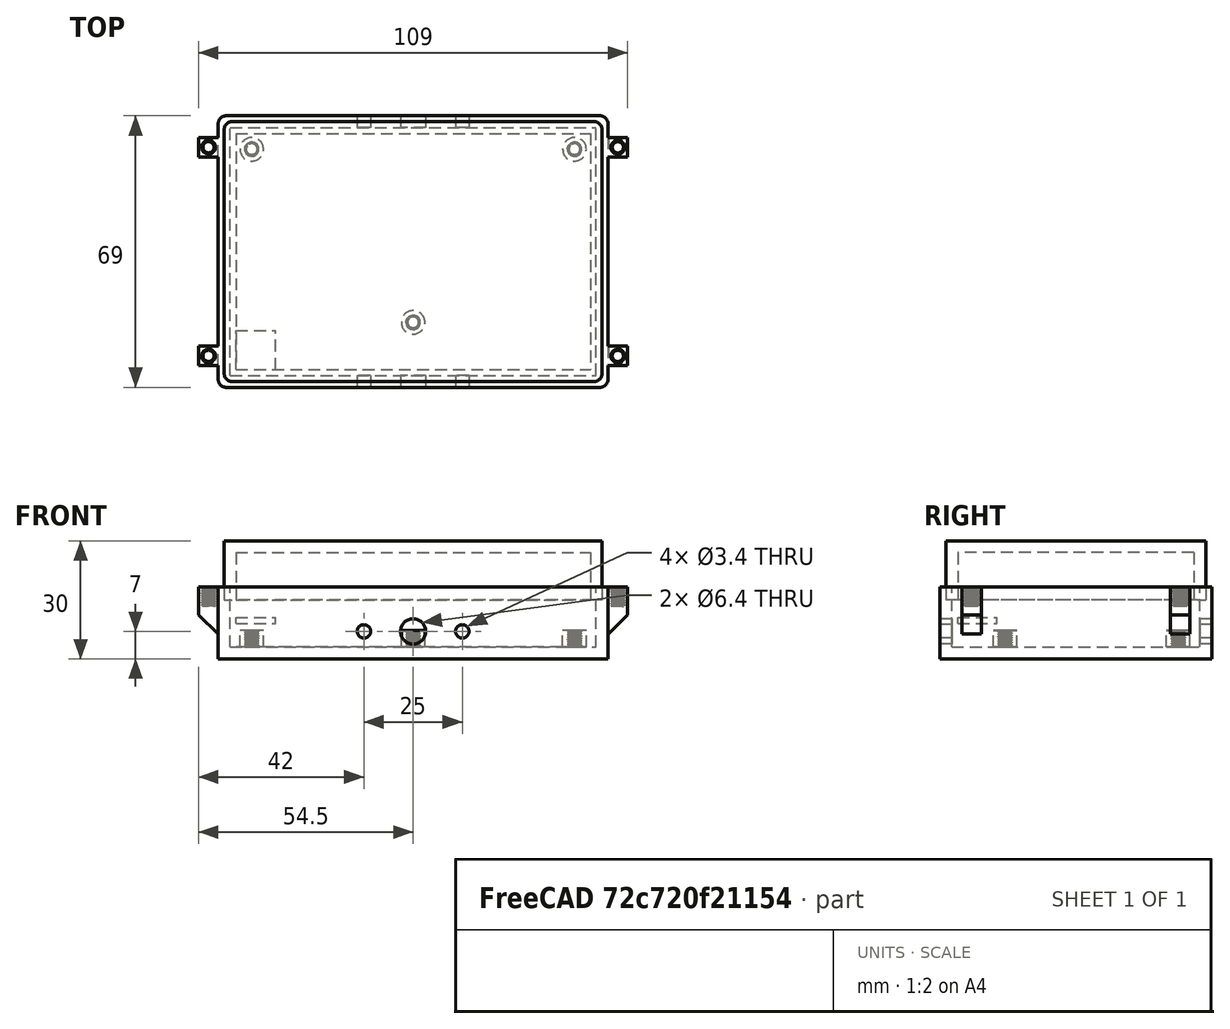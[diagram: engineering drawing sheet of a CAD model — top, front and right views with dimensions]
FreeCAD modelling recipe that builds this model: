
FCSTD DOCUMENT  (FreeCAD 0.18.4R)
Label: PCB_CASE_VPLOTTER
License: All rights reserved
LicenseURL: http://en.wikipedia.org/wiki/All_rights_reserved
objects: Part::Cylinder×9, Part::Box×7, Part::FeaturePython×7, Part::Cut×6, Part::MultiFuse×5, Part::Chamfer×4, Part::Thickness×2, Part::Fillet×2
note: 42 computed .brp shape members not serialized (recipe doc carries the construction recipe); baked Part::Feature solids carry a one-line shape summary decoded from their .brp

FEATURE [Part::Box] Box  label="Cube"
  AttacherType = Attacher::AttachEngine3D
  Height = 15.3
  Length = 93
  Placement = pos=(-1.5,-1.5,0) rot=(0,0,1;0rad)
  Width = 63
FEATURE [Part::Cylinder] Cylinder
  Angle = 360
  AttacherType = Attacher::AttachEngine3D
  Height = 4.8
  Placement = pos=(86,56,0) rot=(0,0,1;0rad)
  Radius = 3
FEATURE [Part::Cylinder] Cylinder001
  Angle = 360
  AttacherType = Attacher::AttachEngine3D
  Height = 4.8
  Placement = pos=(4,56,0) rot=(0,0,1;0rad)
  Radius = 3
FEATURE [Part::Cylinder] Cylinder002
  Angle = 360
  AttacherType = Attacher::AttachEngine3D
  Height = 4.8
  Placement = pos=(45,12,0) rot=(0,0,1;0rad)
  Radius = 3
FEATURE [Part::Thickness] Thickness
  Faces = -> Box [Face6]
  Intersection = false
  Join = 2
  Mode = 0
  SelfIntersection = false
  Value = 3
FEATURE [Part::Cylinder] Cylinder003
  Angle = 360
  AttacherType = Attacher::AttachEngine3D
  Height = 10
  Placement = pos=(32.5,4,4) rot=(1,0,0;1.5708rad)
  Radius = 1.7
FEATURE [Part::Cylinder] Cylinder004
  Angle = 360
  AttacherType = Attacher::AttachEngine3D
  Height = 10
  Placement = pos=(57.5,4,4) rot=(1,0,0;1.5708rad)
  Radius = 1.7
FEATURE [Part::Cylinder] Cylinder007
  Angle = 360
  AttacherType = Attacher::AttachEngine3D
  Height = 10
  Placement = pos=(45,4,4) rot=(1,0,0;1.5708rad)
  Radius = 3.2
FEATURE [Part::Cylinder] Cylinder008
  Angle = 360
  AttacherType = Attacher::AttachEngine3D
  Height = 10
  Placement = pos=(57.5,67,4) rot=(1,0,0;1.5708rad)
  Radius = 1.7
FEATURE [Part::Cylinder] Cylinder010
  Angle = 360
  AttacherType = Attacher::AttachEngine3D
  Height = 10
  Placement = pos=(45,67,4) rot=(1,0,0;1.5708rad)
  Radius = 3.2
FEATURE [Part::Cylinder] Cylinder011
  Angle = 360
  AttacherType = Attacher::AttachEngine3D
  Height = 10
  Placement = pos=(32.5,67,4) rot=(1,0,0;1.5708rad)
  Radius = 1.7
FEATURE [Part::Box] Box001  label="Cube001"
  AttacherType = Attacher::AttachEngine3D
  Height = 12
  Length = 5
  Placement = pos=(-9,0,0) rot=(0,0,1;0rad)
  Width = 5
FEATURE [Part::Chamfer] Chamfer
  Base = -> Box001
  Edges = 1 edges r=4.9: [Edge4]
  Placement = pos=(1,1,0) rot=(0,0,1;0rad)
FEATURE [Part::FeaturePython] ScrewTap  label="(M3.5)x20.0-ScrewTap"  # Fasteners workbench fastener (typed FeaturePython)
  Placement = pos=(-5.5,3.5,27.5) rot=(0,0,1;0rad)
  diameter = 5
  invert = false
  length = 20
  matchOuter = false
  offset = 0
  thread = true
FEATURE [Part::Cut] Cut
  Base = -> Chamfer
  Placement = pos=(-1.5,0,3.3) rot=(0,0,1;0rad)
  Tool = -> ScrewTap
FEATURE [Part::Box] Box002  label="Cube002"
  AttacherType = Attacher::AttachEngine3D
  Height = 12
  Length = 5
  Placement = pos=(-9,0,0) rot=(0,0,1;0rad)
  Width = 5
FEATURE [Part::Chamfer] Chamfer001
  Base = -> Box002
  Edges = 1 edges r=4.9: [Edge4]
  Placement = pos=(1,1,0) rot=(0,0,1;0rad)
FEATURE [Part::FeaturePython] ScrewTap001  label="(M3.5)x20.0-ScrewTap001"  # Fasteners workbench fastener (typed FeaturePython)
  Placement = pos=(-5.5,3.5,27.5) rot=(0,0,1;0rad)
  diameter = 5
  invert = false
  length = 20
  matchOuter = false
  offset = 0
  thread = true
FEATURE [Part::Cut] Cut001
  Base = -> Chamfer001
  Placement = pos=(-1.5,53,3.3) rot=(0,0,1;0rad)
  Tool = -> ScrewTap001
FEATURE [Part::Box] Box003  label="Cube003"
  AttacherType = Attacher::AttachEngine3D
  Height = 12
  Length = 5
  Placement = pos=(-9,0,0) rot=(0,0,1;0rad)
  Width = 5
FEATURE [Part::Chamfer] Chamfer002
  Base = -> Box003
  Edges = 1 edges r=4.9: [Edge4]
  Placement = pos=(1,1,0) rot=(0,0,1;0rad)
FEATURE [Part::FeaturePython] ScrewTap002  label="(M3.5)x20.0-ScrewTap002"  # Fasteners workbench fastener (typed FeaturePython)
  Placement = pos=(-5.5,3.5,27.5) rot=(0,0,1;0rad)
  diameter = 5
  invert = false
  length = 20
  matchOuter = false
  offset = 0
  thread = true
FEATURE [Part::Cut] Cut002
  Base = -> Chamfer002
  Placement = pos=(91.5,60,3.3) rot=(0,0,1;3.14159rad)
  Tool = -> ScrewTap002
FEATURE [Part::FeaturePython] ScrewTap003  label="(M3.5)x20.0-ScrewTap003"  # Fasteners workbench fastener (typed FeaturePython)
  Placement = pos=(-5.5,3.5,27.5) rot=(0,0,1;0rad)
  diameter = 5
  invert = false
  length = 20
  matchOuter = false
  offset = 0
  thread = true
FEATURE [Part::Box] Box004  label="Cube004"
  AttacherType = Attacher::AttachEngine3D
  Height = 12
  Length = 5
  Placement = pos=(-9,0,0) rot=(0,0,1;0rad)
  Width = 5
FEATURE [Part::Chamfer] Chamfer003
  Base = -> Box004
  Edges = 1 edges r=4.9: [Edge4]
  Placement = pos=(1,1,0) rot=(0,0,1;0rad)
FEATURE [Part::Cut] Cut003
  Base = -> Chamfer003
  Placement = pos=(91.5,7,3.3) rot=(0,0,1;3.14159rad)
  Tool = -> ScrewTap003
FEATURE [Part::Fillet] Fillet
  Base = -> Thickness
  Edges = 4 edges r=2: [Edge17,Edge19,Edge20,Edge22]
FEATURE [Part::Box] Box005  label="Cube005"
  AttacherType = Attacher::AttachEngine3D
  Height = 12
  Length = 90
  Width = 60
FEATURE [Part::Thickness] Thickness001
  Faces = -> Box005 [Face6]
  Intersection = false
  Join = 2
  Mode = 0
  SelfIntersection = false
  Value = 3
FEATURE [Part::Fillet] Fillet001
  Base = -> Thickness001
  Edges = 4 edges r=2: [Edge17,Edge19,Edge20,Edge22]
  Placement = pos=(0,60,24) rot=(1,0,0;3.14159rad)
FEATURE [Part::MultiFuse] Fusion
  Shapes = -> [Fillet,Cut003,Cut002,Cut001,Cut]
FEATURE [Part::MultiFuse] Fusion001
  Shapes = -> [Cylinder011,Cylinder010,Cylinder008,Cylinder007,Cylinder004,Cylinder003]
FEATURE [Part::Cut] Cut004
  Base = -> Fusion
  Tool = -> Fusion001
FEATURE [Part::FeaturePython] ScrewTap004  label="(M3.5)x7.0-ScrewTap"  # Fasteners workbench fastener (typed FeaturePython)
  Placement = pos=(45,12,7) rot=(0,0,1;0rad)
  diameter = 5
  invert = false
  length = 7
  matchOuter = false
  offset = 0
  thread = true
FEATURE [Part::FeaturePython] ScrewTap005  label="(M3.5)x7.0-ScrewTap001"  # Fasteners workbench fastener (typed FeaturePython)
  Placement = pos=(4,56,7) rot=(0,0,1;0rad)
  diameter = 5
  invert = false
  length = 7
  matchOuter = false
  offset = 0
  thread = true
FEATURE [Part::FeaturePython] ScrewTap006  label="(M3.5)x7.0-ScrewTap002"  # Fasteners workbench fastener (typed FeaturePython)
  Placement = pos=(86,56,7) rot=(0,0,1;0rad)
  diameter = 5
  invert = false
  length = 7
  matchOuter = false
  offset = 0
  thread = true
FEATURE [Part::MultiFuse] Fusion002
  Shapes = -> [ScrewTap004,ScrewTap005,ScrewTap006]
FEATURE [Part::MultiFuse] Fusion003
  Shapes = -> [Cylinder,Cylinder001,Cylinder002]
FEATURE [Part::Cut] Cut005
  Base = -> Fusion003
  Tool = -> Fusion002
FEATURE [Part::MultiFuse] Fusion004
  Shapes = -> [Cut004,Cut005]
FEATURE [Part::Box] Box006  label="Cube006"
  AttacherType = Attacher::AttachEngine3D
  Height = 1.6
  Length = 10
  Placement = pos=(0,0,6) rot=(0,0,1;0rad)
  Width = 10
